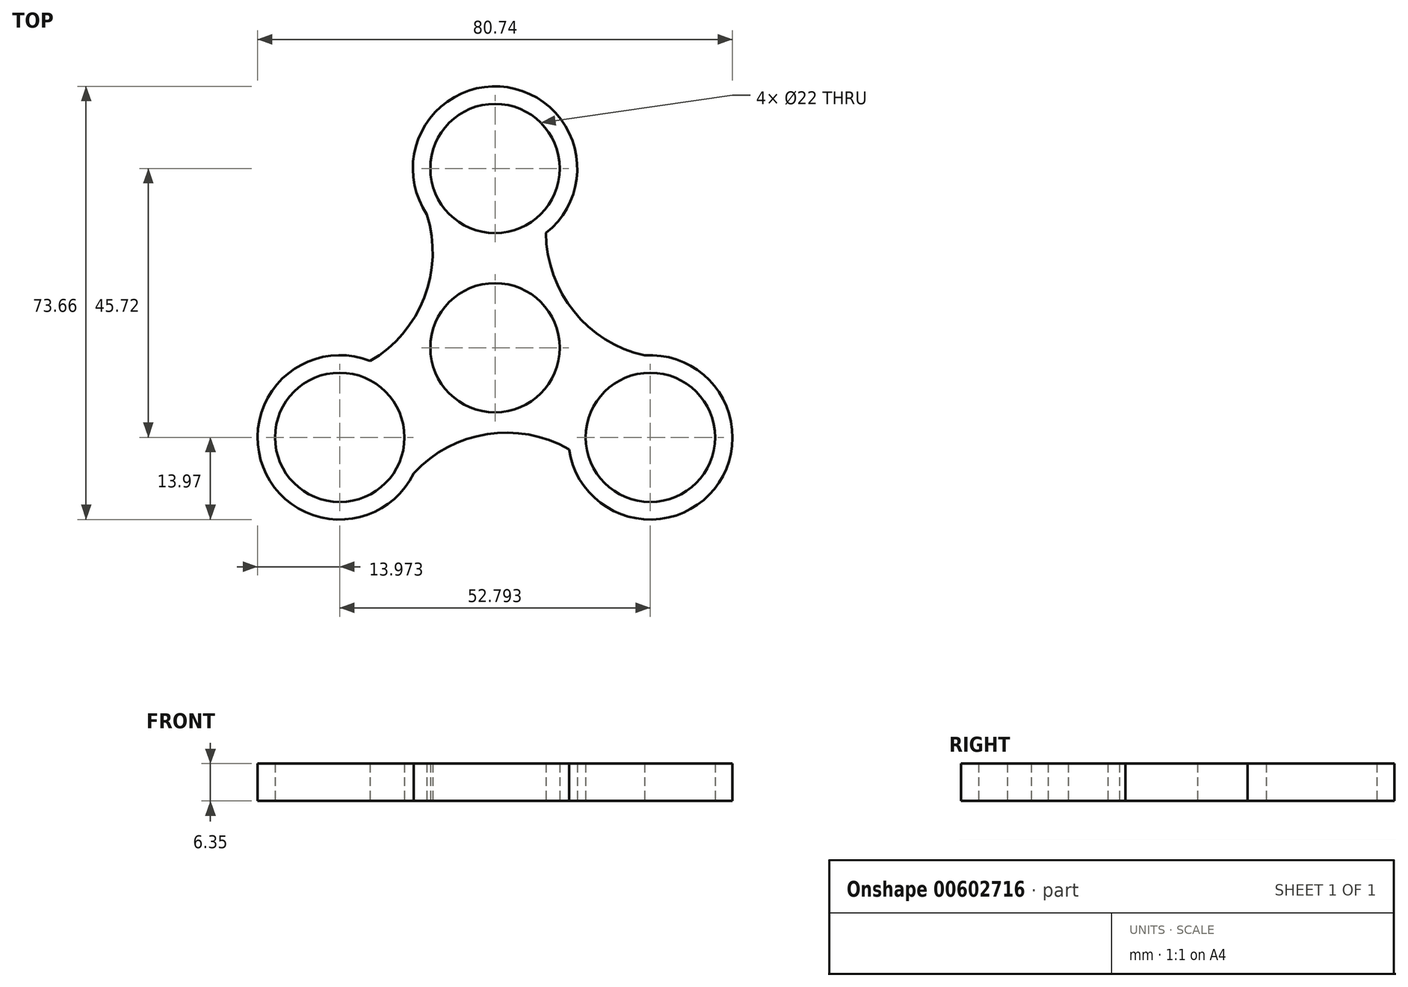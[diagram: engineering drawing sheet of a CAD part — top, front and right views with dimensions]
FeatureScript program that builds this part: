
annotation { "Feature Type Name" : "Feature", "Feature Type Description" : "" }
export const myFeature = defineFeature(function(context is Context, id is Id, definition is map)
    precondition{}
    {
        {
            var Q0;
            Q0=qCreatedBy(makeId("Top.planeOp"),FACE);
            var sketch = newSketch(context, id + "F0", { "sketchPlane" : qUnion([Q0])});
            skCircle(sketch, "E0", {"center": v(0, 0) * mm, "radius": 44.45 * mm});
            skCircle(sketch, "E1", {"center": v(0, 0) * mm, "radius": 11 * mm});
            skLineSegment(sketch, "E2", {"start": v(0, 0) * mm, "end": v(0, 30.48) * mm});
            skCircle(sketch, "E3", {"center": v(0, 30.48) * mm, "radius": 11 * mm});
            skCircle(sketch, "E4.1.0", {"center": v(-26.4, -15.24) * mm, "radius": 11 * mm});
            skCircle(sketch, "E4.2.0", {"center": v(26.4, -15.24) * mm, "radius": 11 * mm});
            skCircle(sketch, "E5", {"center": v(-26.4, -15.24) * mm, "radius": 13.97 * mm});
            skCircle(sketch, "E6", {"center": v(26.4, -15.24) * mm, "radius": 13.97 * mm});
            skCircle(sketch, "E7", {"center": v(0, 30.48) * mm, "radius": 13.97 * mm});
            skCircle(sketch, "E8", {"center": v(0, 0) * mm, "radius": 13.97 * mm});
            skArc(sketch, "E9", {"start": v(-21.23, -2.26) * mm, "mid": v(-12.05, 8.51) * mm, "end": v(-11.58, 22.66) * mm});
            skArc(sketch, "E10.1.0", {"start": v(12.57, -17.26) * mm, "mid": v(-1.35, -14.7) * mm, "end": v(-13.84, -21.35) * mm});
            skArc(sketch, "E10.2.0", {"start": v(8.66, 19.52) * mm, "mid": v(13.4, 6.18) * mm, "end": v(25.41, -1.3) * mm});
            skSolve(sketch);
        }
        {
            var Q0;
            Q0=makeQuery(id+"F0.imprint","IMPRINT",FACE,{"disambiguationData":[TD([[makeQuery(id+"F0.imprint","IMPRINT",EDGE,{"derivedFrom":sQuery(id+"F0.wireOp",EDGE,"E3")}),-1.0]])]});
            var Q1;
            Q1=makeQuery(id+"F0.imprint","IMPRINT",FACE,{"disambiguationData":[TD([[makeQuery(id+"F0.imprint","IMPRINT",EDGE,{"derivedFrom":sQuery(id+"F0.wireOp",EDGE,"E4.1.0")}),-1.0]])]});
            var Q2;
            Q2=makeQuery(id+"F0.imprint","IMPRINT",FACE,{"disambiguationData":[TD([[makeQuery(id+"F0.imprint","IMPRINT",EDGE,{"derivedFrom":sQuery(id+"F0.wireOp",EDGE,"E4.2.0")}),-1.0]])]});
            var Q3;
            Q3=makeQuery(id+"F0.imprint","IMPRINT",FACE,{"disambiguationData":[TD([[makeQuery(id+"F0.imprint","IMPRINT",EDGE,{"derivedFrom":sQuery(id+"F0.wireOp",EDGE,"E8")}),-1.0]])]});
            var Q4;
            Q4=makeQuery(id+"F0.imprint","IMPRINT",FACE,{"disambiguationData":[TD([[makeQuery(id+"F0.imprint","IMPRINT",EDGE,{"derivedFrom":sQuery(id+"F0.wireOp",EDGE,"E1")}),-1.0]])]});
            extrude(context, id + "F1", {"entities" : qUnion([Q0, Q1, Q2, Q3, Q4]), "depth" : 6.35 * mm, "offsetDistance" : 25.4 * mm});
        }
    });
